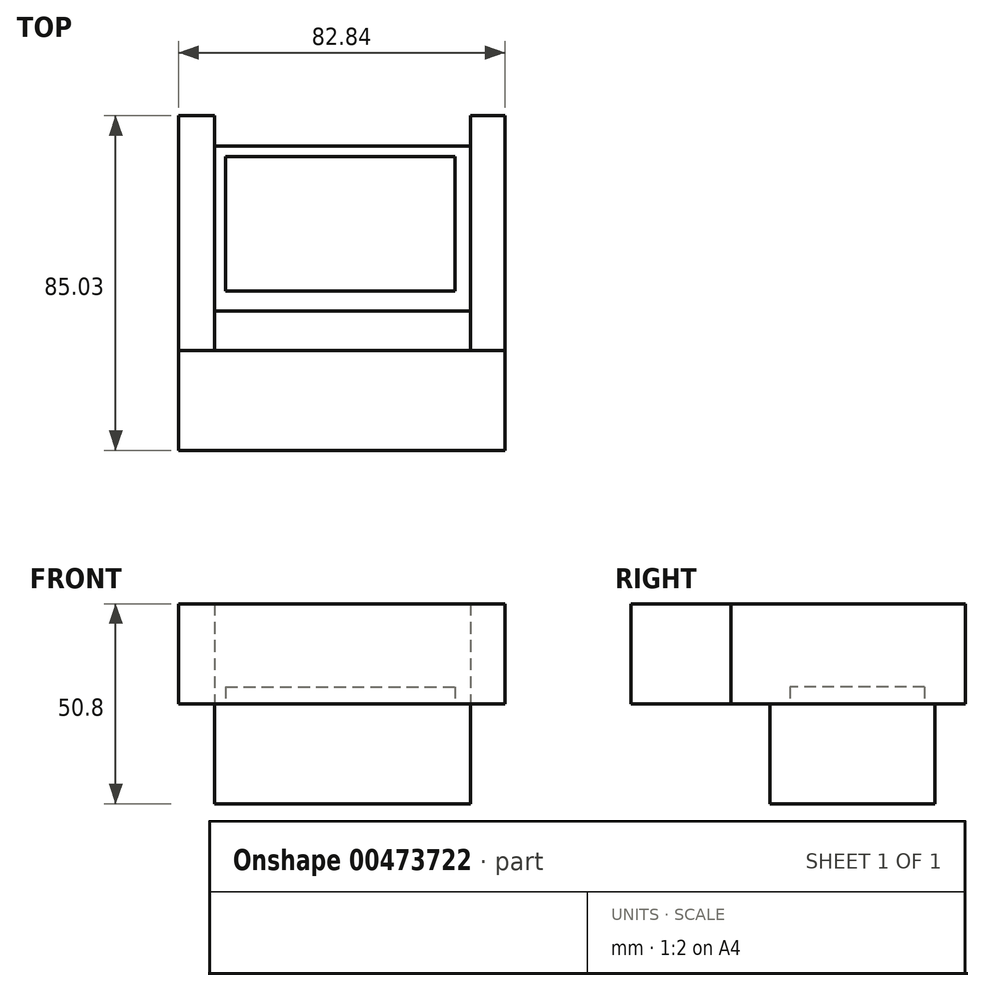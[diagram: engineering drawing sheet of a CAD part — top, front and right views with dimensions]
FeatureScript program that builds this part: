
annotation { "Feature Type Name" : "Feature", "Feature Type Description" : "" }
export const myFeature = defineFeature(function(context is Context, id is Id, definition is map)
    precondition{}
    {
        {
            var Q0;
            Q0=qCreatedBy(makeId("Top.planeOp"),FACE);
            var sketch = newSketch(context, id + "F0", { "sketchPlane" : qUnion([Q0])});
            skLineSegment(sketch, "E0.bottom", {"start": v(-52.18, 30) * mm, "end": v(-43.12, 30) * mm});
            skLineSegment(sketch, "E0.top", {"start": v(-52.18, -29.63) * mm, "end": v(-43.12, -29.63) * mm});
            skLineSegment(sketch, "E0.left", {"start": v(-52.18, 30) * mm, "end": v(-52.18, -29.63) * mm});
            skLineSegment(sketch, "E0.right", {"start": v(-43.12, 30) * mm, "end": v(-43.12, -29.63) * mm});
            skPoint(sketch, "E1.oppositeSnap0", {"position": v(-47.65, -29.63) * mm});
            skLineSegment(sketch, "E1.bottom", {"start": v(21.98, 30) * mm, "end": v(30.66, 30) * mm});
            skLineSegment(sketch, "E1.top", {"start": v(21.98, -29.63) * mm, "end": v(30.66, -29.63) * mm});
            skLineSegment(sketch, "E1.left", {"start": v(21.98, 30) * mm, "end": v(21.98, -29.63) * mm});
            skLineSegment(sketch, "E1.right", {"start": v(30.66, 30) * mm, "end": v(30.66, -29.63) * mm});
            skLineSegment(sketch, "E2.bottom", {"start": v(-43.12, 22.27) * mm, "end": v(21.98, 22.27) * mm});
            skLineSegment(sketch, "E2.top", {"start": v(-43.12, -19.63) * mm, "end": v(21.98, -19.63) * mm});
            skLineSegment(sketch, "E2.left", {"start": v(-43.12, 22.27) * mm, "end": v(-43.12, -19.63) * mm});
            skLineSegment(sketch, "E2.right", {"start": v(21.98, 22.27) * mm, "end": v(21.98, -19.63) * mm});
            skLineSegment(sketch, "E3.bottom", {"start": v(-40.29, 19.63) * mm, "end": v(18.02, 19.63) * mm});
            skLineSegment(sketch, "E3.top", {"start": v(-40.29, -14.53) * mm, "end": v(18.02, -14.53) * mm});
            skLineSegment(sketch, "E3.left", {"start": v(-40.29, 19.63) * mm, "end": v(-40.29, -14.53) * mm});
            skLineSegment(sketch, "E3.right", {"start": v(18.02, 19.63) * mm, "end": v(18.02, -14.53) * mm});
            skSolve(sketch);
        }
        {
            var Q0;
            {var subQ1=sQuery(id+"F0.wireOp",EDGE,"E0.bottom");Q0=makeQuery(id+"F0.imprint","IMPRINT",FACE,{"disambiguationData":[TD([[makeQuery(id+"F0.imprint","IMPRINT",EDGE,{"derivedFrom":subQ1}),-1.0]])]});}
            var Q1;
            {var subQ3=sQuery(id+"F0.wireOp",EDGE,"E1.bottom");Q1=makeQuery(id+"F0.imprint","IMPRINT",FACE,{"disambiguationData":[TD([[makeQuery(id+"F0.imprint","IMPRINT",EDGE,{"derivedFrom":subQ3}),-1.0]])]});}
            extrude(context, id + "F1", {"entities" : qUnion([Q0, Q1]), "depth" : 25.4 * mm});
        }
        {
            var Q0;
            Q0=makeQuery(id+"F0.imprint","IMPRINT",FACE,{"disambiguationData":[TD([[makeQuery(id+"F0.imprint","IMPRINT",EDGE,{"derivedFrom":sQuery(id+"F0.wireOp",EDGE,"E2.bottom")}),-1.0]])]});
            var Q1;
            Q1=makeQuery(id+"F0.imprint","IMPRINT",FACE,{"disambiguationData":[TD([[makeQuery(id+"F0.imprint","IMPRINT",EDGE,{"derivedFrom":sQuery(id+"F0.wireOp",EDGE,"E3.bottom")}),-1.0]])]});
            extrude(context, id + "F2", {"entities" : qUnion([Q0, Q1]), "oppositeDirection" : true, "depth" : 25.4 * mm});
        }
        {
            var Q0;
            Q0=makeQuery(id+"F0.imprint","IMPRINT",FACE,{"disambiguationData":[TD([[makeQuery(id+"F0.imprint","IMPRINT",EDGE,{"derivedFrom":sQuery(id+"F0.wireOp",EDGE,"E3.bottom")}),-1.0]])]});
            extrude(context, id + "F3", {"entities" : qUnion([Q0]), "depth" : 4.32 * mm});
        }
        {
            var Q0;
            Q0=makeQuery(id+"F1.opExtrude","SWEPT_FACE",FACE,{"disambiguationData":[OSD([sQuery(id+"F0.wireOp",EDGE,"E0.top")])]});
            var sketch = newSketch(context, id + "F4", { "sketchPlane" : qUnion([Q0])});
            skLineSegment(sketch, "E4.bottom", {"start": v(-52.18, 0) * mm, "end": v(30.66, 0) * mm});
            skLineSegment(sketch, "E4.top", {"start": v(-52.18, 25.4) * mm, "end": v(30.66, 25.4) * mm});
            skLineSegment(sketch, "E4.left", {"start": v(-52.18, 0) * mm, "end": v(-52.18, 25.4) * mm});
            skLineSegment(sketch, "E4.right", {"start": v(30.66, 0) * mm, "end": v(30.66, 25.4) * mm});
            skSolve(sketch);
        }
        {
            var Q0;
            Q0 = qSketchRegion(id + "F4", true);
            extrude(context, id + "F5", {"entities" : qUnion([Q0]), "depth" : 25.4 * mm});
        }
    });
